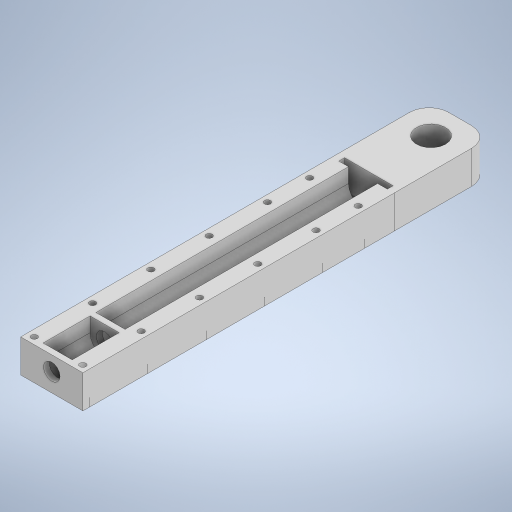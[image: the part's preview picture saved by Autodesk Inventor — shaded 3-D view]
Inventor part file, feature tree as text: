
AUTODESK INVENTOR PART (.ipt)
format: ipt  version: 2023 (Build 270158000, 158)  size: 454,144 bytes
history: native  units: mm
features: sketch x10, extrude x7, hole x3, fillet x1, projected_geometry x1
ambient origin geometry x8: Origin, YZ Plane, XZ Plane, XY Plane, X Axis, Y Axis, Z Axis, Center Point
bodies: Solid1 (feature_tree)
feature tree (22):
  extrude  "Extrusion1"  Depth=24.2mm TaperAngle=0.0deg
  extrude  "Extrusion3"  Depth=2.0mm
  extrude  "Extrusion4"  Depth=3.0mm TaperAngle=0.0deg
  extrude  "Extrusion5"  Depth=130.0mm TaperAngle=0.0deg
  hole  "Hole1"  [1 undecoded]
  hole  "Hole3"  [1 undecoded]
  extrude  "Extrusion6"  Depth=3.5mm
  extrude  "Extrusion7"  Depth=6.0mm
  fillet  "Fillet1"  Radius=50.0mm
  hole  "Hole4"  [1 undecoded]
  extrude  "Extrusion8"  Depth=20.0mm
  sketch  "Sketch1"  dims[d0=15.0mm d3=24.2mm d4=0.0mm]
  sketch  "Sketch2"  dims[d5=32.0mm d6=2.0mm]
  projected_geometry  "Projected Loop1"
  sketch  "Sketch4"  dims[d10=8.5mm d11=3.0mm d12=0.0mm]
  sketch  "Sketch5"  dims[d13=3.0mm d14=0.0mm d15=130.0mm d16=0.0mm]
  sketch  "Sketch6"  dims[d17=3.5mm d18=3.5mm]
  sketch  "Sketch7"  dims[d19=2.38125mm d20=6.0mm d21=4.0mm d22=2.0mm d23=90.0deg d24=10.0mm d25=20.594885mm d27=3.5mm]
  sketch  "Sketch8"  dims[d42=50.0mm d44=30.0mm d45=10.0mm d47=10.0mm d49=3.5mm]
  sketch  "Sketch9"  dims[d50=15.0mm]
  sketch  "Sketch10"  dims[d51=3.175mm d52=6.0mm d53=4.0mm d54=2.0mm d55=90.0deg d56=10.0mm d57=20.594885mm d58=6.0mm]
  sketch  "Sketch11"  dims[d59=20.0mm d61=25.0mm d62=10.0mm d64=10.0mm d66=50.0mm d68=30.0mm d69=10.0mm d71=10.0mm d73=50.0mm d75=30.0mm d76=10.0mm d78=10.0mm d80=20.0mm d82=21.5mm d83=10.0mm d85=10.0mm d87=4.0mm d88=0.0mm d89=50.0mm d90=0.0mm d91=10.0mm d94=15.0mm d95=15.0mm d96=6.0mm d97=4.0mm d98=2.0mm d99=90.0deg d100=8.0mm d101=20.594885mm d102=25.0mm d103=3.0mm d104=15.0mm d105=0.0mm]
note: 3 required parameter values undecoded (feature->parameter linkage not recoverable at this tier; creation-order binding heuristic only, values carry confidence <= 0.55)
